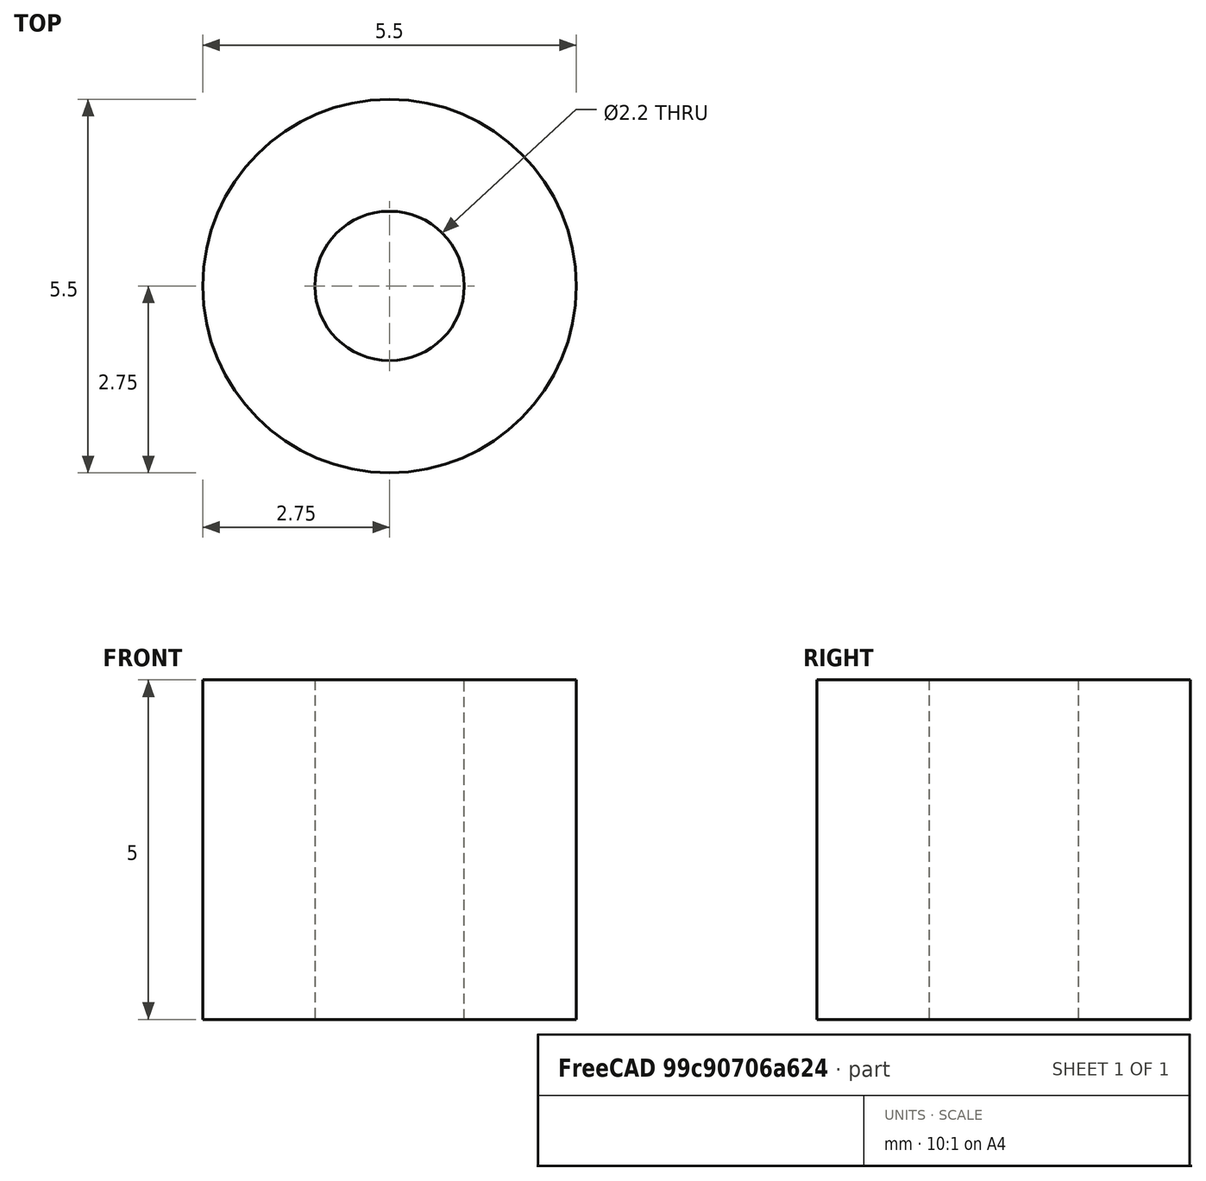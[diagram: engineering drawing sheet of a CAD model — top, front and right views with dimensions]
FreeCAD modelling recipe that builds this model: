
FCSTD DOCUMENT  (FreeCAD 0.18R13959 (Git))
Label: Spacer_M2x5mm
License: CreativeCommons Attribution-NonCommercial-ShareAlike
LicenseURL: http://creativecommons.org/licenses/by-nc-sa/4.0/
objects: Sketcher::SketchObject×1, PartDesign::Pad×1, PartDesign::Body×1, Mesh::Feature×1
note: 4 computed .brp shape members not serialized (recipe doc carries the construction recipe); baked Part::Feature solids carry a one-line shape summary decoded from their .brp

FEATURE [Sketcher::SketchObject] Sketch
  MapMode = 5
  Support = -> [XY_Plane]
  sketch-geometry (2):
    g0: Circle CenterX=0 CenterY=0 CenterZ=0 NormalX=0 NormalY=0 NormalZ=1 AngleXU=0 Radius=2.75
    g1: Circle CenterX=0 CenterY=0 CenterZ=0 NormalX=0 NormalY=0 NormalZ=1 AngleXU=0 Radius=1.1
  constraints (4):
    c: Coincident(g0,g-1)
    c: Radius(g0) = 2.75
    c: Coincident(g1,g-1)
    c: Radius(g1) = 1.1
FEATURE [PartDesign::Pad] Pad
  Length = 5
  Length2 = 100
  Profile = -> Sketch
  Type = 0
FEATURE [PartDesign::Body] Body
  Group = -> [Sketch,Pad]
  Origin = -> Origin
  Tip = -> Pad
FEATURE [Mesh::Feature] Mesh  label="Pad (Meshed)"
